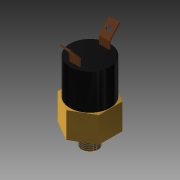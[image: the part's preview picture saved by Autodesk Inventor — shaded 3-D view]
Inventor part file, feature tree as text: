
AUTODESK INVENTOR PART (.ipt)
format: ipt  version: 2018 (Build 220112000, 112)  size: 169,984 bytes
history: native  units: mm (DEFAULTED — no unit token found)
features: extrude x6, sketch x6, projected_geometry x4, mirror x1, thread x1, chamfer x1, fillet x1
ambient origin geometry x8: Origin, YZ Plane, XZ Plane, XY Plane, X Axis, Y Axis, Z Axis, Center Point
bodies: Solid1 (feature_tree)
feature tree (20):
  extrude  "Extrusion1"  Depth=15.875mm TaperAngle=0.0deg
  extrude  "Extrusion2"  Depth=11.049mm TaperAngle=0.0deg
  extrude  "Extrusion3"  Depth=19.9898mm TaperAngle=0.0deg
  extrude  "Extrusion4"  Depth=21.971mm TaperAngle=0.0deg
  extrude  "Extrusion5"  Depth=0.762mm
  extrude  "Extrusion6"  Depth=3.175mm
  mirror  "Mirror1"
  thread  "Thread1"  [1 undecoded]
  chamfer  "Chamfer1"  Distance=6.35mm
  fillet  "Fillet1"  Radius=6.35mm
  sketch  "Sketch1"  dims[d0=25.4mm d1=15.875mm d2=0.0mm]
  sketch  "Sketch2"  dims[d3=10.16mm d4=11.049mm d5=0.0mm]
  projected_geometry  "Projected Loop1"
  sketch  "Sketch3"  dims[d6=3.175mm d7=19.9898mm d8=0.0mm]
  sketch  "Sketch4"  dims[d9=24.765mm d10=21.971mm d11=0.0mm]
  projected_geometry  "Projected Loop2"
  sketch  "Sketch5"  dims[d12=19.05mm d13=0.762mm]
  projected_geometry  "Projected Loop3"
  sketch  "Sketch6"  dims[d14=0.762mm d15=4.699mm d17=9.398mm d18=6.35mm d19=0.0mm d20=6.35mm d21=0.0mm d22=25.4mm d23=0.0mm d24=1.0mm d25=3.175mm d26=45.0deg d27=3.175mm]
  projected_geometry  "Projected Loop4"
note: 1 required parameter value undecoded (feature->parameter linkage not recoverable at this tier; creation-order binding heuristic only, values carry confidence <= 0.55)
